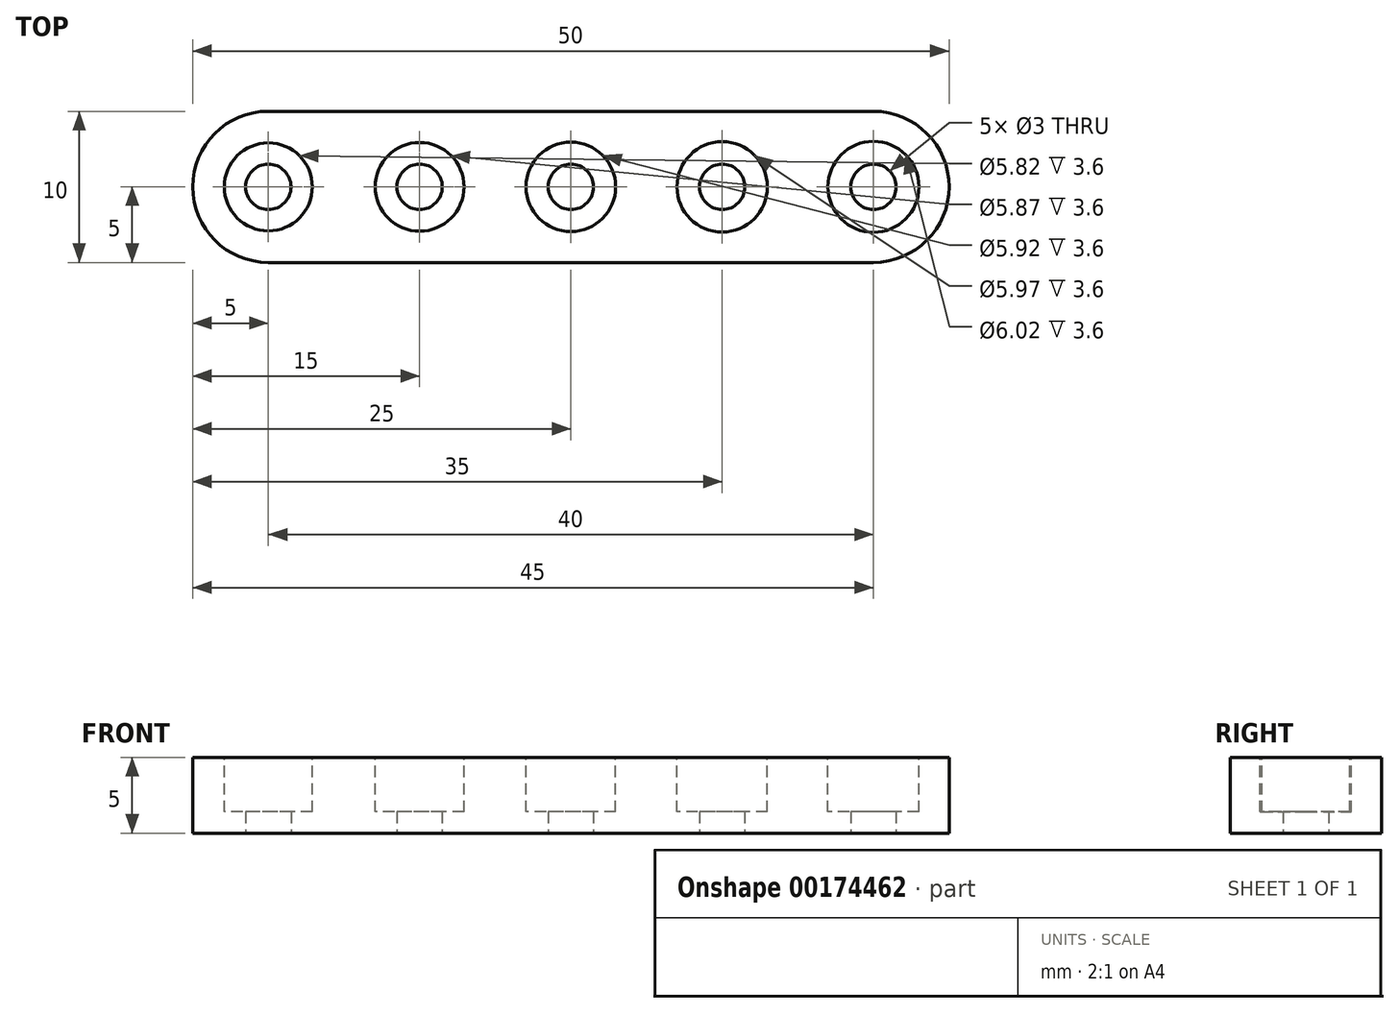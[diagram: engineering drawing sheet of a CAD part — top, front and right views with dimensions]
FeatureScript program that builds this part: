
annotation { "Feature Type Name" : "Feature", "Feature Type Description" : "" }
export const myFeature = defineFeature(function(context is Context, id is Id, definition is map)
    precondition{}
    {
        {
            var Q0;
            Q0=qCreatedBy(makeId("Top.planeOp"),FACE);
            var sketch = newSketch(context, id + "F0", { "sketchPlane" : qUnion([Q0])});
            skLineSegment(sketch, "E0.bottom", {"start": v(0, 0) * mm, "end": v(50, 0) * mm});
            skLineSegment(sketch, "E0.top", {"start": v(0, 10) * mm, "end": v(50, 10) * mm});
            skLineSegment(sketch, "E0.left", {"start": v(0, 0) * mm, "end": v(0, 10) * mm});
            skLineSegment(sketch, "E0.right", {"start": v(50, 0) * mm, "end": v(50, 10) * mm});
            skSolve(sketch);
        }
        {
            var Q0;
            Q0=makeQuery(id+"F0.imprint","IMPRINT",FACE,{"disambiguationData":[TD([[makeQuery(id+"F0.imprint","IMPRINT",EDGE,{"derivedFrom":sQuery(id+"F0.wireOp",EDGE,"E0.bottom")}),1.0]])]});
            extrude(context, id + "F1", {"entities" : qUnion([Q0]), "depth" : 5 * mm});
        }
        {
            var Q0;
            Q0=makeQuery(id+"F1.opExtrude","CAP_FACE",FACE,{"disambiguationData":[OSD([sQuery(id+"F0.wireOp",EDGE,"E0.bottom"),sQuery(id+"F0.wireOp",EDGE,"E0.top"),sQuery(id+"F0.wireOp",EDGE,"E0.left"),sQuery(id+"F0.wireOp",EDGE,"E0.right")])],"isStart":true});
            var sketch = newSketch(context, id + "F2", { "sketchPlane" : qUnion([Q0])});
            skLineSegment(sketch, "E1", {"start": v(0, -5) * mm, "end": v(5, -5) * mm, "construction": true});
            skLineSegment(sketch, "E2", {"start": v(5, -5) * mm, "end": v(15, -5) * mm, "construction": true});
            skLineSegment(sketch, "E3", {"start": v(15, -5) * mm, "end": v(25, -5) * mm, "construction": true});
            skLineSegment(sketch, "E4", {"start": v(25, -5) * mm, "end": v(35, -5) * mm, "construction": true});
            skLineSegment(sketch, "E5", {"start": v(35, -5) * mm, "end": v(45, -5) * mm, "construction": true});
            skCircle(sketch, "E6", {"center": v(5, -5) * mm, "radius": 1.5 * mm});
            skCircle(sketch, "E7", {"center": v(15, -5) * mm, "radius": 1.5 * mm});
            skCircle(sketch, "E8", {"center": v(25, -5) * mm, "radius": 1.5 * mm});
            skCircle(sketch, "E9", {"center": v(35, -5) * mm, "radius": 1.5 * mm});
            skCircle(sketch, "E10", {"center": v(45, -5) * mm, "radius": 1.5 * mm});
            skSolve(sketch);
        }
        {
            var Q0;
            Q0=makeQuery(id+"F2.imprint","IMPRINT",FACE,{"disambiguationData":[TD([[makeQuery(id+"F2.imprint","IMPRINT",EDGE,{"derivedFrom":sQuery(id+"F2.wireOp",EDGE,"E6")}),1.0]])]});
            var Q1;
            Q1=makeQuery(id+"F2.imprint","IMPRINT",FACE,{"disambiguationData":[TD([[makeQuery(id+"F2.imprint","IMPRINT",EDGE,{"derivedFrom":sQuery(id+"F2.wireOp",EDGE,"E7")}),1.0]])]});
            var Q2;
            Q2=makeQuery(id+"F2.imprint","IMPRINT",FACE,{"disambiguationData":[TD([[makeQuery(id+"F2.imprint","IMPRINT",EDGE,{"derivedFrom":sQuery(id+"F2.wireOp",EDGE,"E8")}),1.0]])]});
            var Q3;
            Q3=makeQuery(id+"F2.imprint","IMPRINT",FACE,{"disambiguationData":[TD([[makeQuery(id+"F2.imprint","IMPRINT",EDGE,{"derivedFrom":sQuery(id+"F2.wireOp",EDGE,"E9")}),1.0]])]});
            var Q4;
            Q4=makeQuery(id+"F2.imprint","IMPRINT",FACE,{"disambiguationData":[TD([[makeQuery(id+"F2.imprint","IMPRINT",EDGE,{"derivedFrom":sQuery(id+"F2.wireOp",EDGE,"E10")}),1.0]])]});
            extrude(context, id + "F3", {"entities" : qUnion([Q0, Q1, Q2, Q3, Q4]), "operationType" : NewBodyOperationType.REMOVE, "endBound" : BoundingType.THROUGH_ALL, "oppositeDirection" : true, "depth" : 2 * mm});
        }
        {
            var Q0;
            Q0=makeQuery(id+"F1.opExtrude","CAP_FACE",FACE,{"disambiguationData":[OSD([sQuery(id+"F0.wireOp",EDGE,"E0.bottom"),sQuery(id+"F0.wireOp",EDGE,"E0.top"),sQuery(id+"F0.wireOp",EDGE,"E0.left"),sQuery(id+"F0.wireOp",EDGE,"E0.right")])],"isStart":false});
            var sketch = newSketch(context, id + "F4", { "sketchPlane" : qUnion([Q0])});
            skCircle(sketch, "E11", {"center": v(5, 5) * mm, "radius": 2.91 * mm});
            skCircle(sketch, "E12", {"center": v(15, 5) * mm, "radius": 2.94 * mm});
            skCircle(sketch, "E13", {"center": v(25, 5) * mm, "radius": 2.96 * mm});
            skCircle(sketch, "E14", {"center": v(35, 5) * mm, "radius": 2.98 * mm});
            skCircle(sketch, "E15", {"center": v(45, 5) * mm, "radius": 3 * mm});
            skSolve(sketch);
        }
        {
            var Q0;
            Q0=makeQuery(id+"F1.opExtrude","SWEPT_EDGE",EDGE,{"disambiguationData":[OSD([sQuery(id+"F0.wireOp",EDGE,"E0.bottom"),sQuery(id+"F0.wireOp",EDGE,"E0.left")])]});
            var Q1;
            Q1=makeQuery(id+"F1.opExtrude","SWEPT_EDGE",EDGE,{"disambiguationData":[OSD([sQuery(id+"F0.wireOp",EDGE,"E0.top"),sQuery(id+"F0.wireOp",EDGE,"E0.left")])]});
            var Q2;
            Q2=makeQuery(id+"F1.opExtrude","SWEPT_EDGE",EDGE,{"disambiguationData":[OSD([sQuery(id+"F0.wireOp",EDGE,"E0.bottom"),sQuery(id+"F0.wireOp",EDGE,"E0.right")])]});
            var Q3;
            Q3=makeQuery(id+"F1.opExtrude","SWEPT_EDGE",EDGE,{"disambiguationData":[OSD([sQuery(id+"F0.wireOp",EDGE,"E0.top"),sQuery(id+"F0.wireOp",EDGE,"E0.right")])]});
            fillet(context, id + "F5", {"entities" : qUnion([Q0, Q1, Q2, Q3]), "radius" : 5 * mm, "tangentPropagation" : true, "allowEdgeOverflow" : false});
        }
        {
            var Q0;
            Q0 = qSketchRegion(id + "F4", true);
            extrude(context, id + "F6", {"entities" : qUnion([Q0]), "operationType" : NewBodyOperationType.REMOVE, "oppositeDirection" : true, "depth" : 3.6 * mm});
        }
    });
